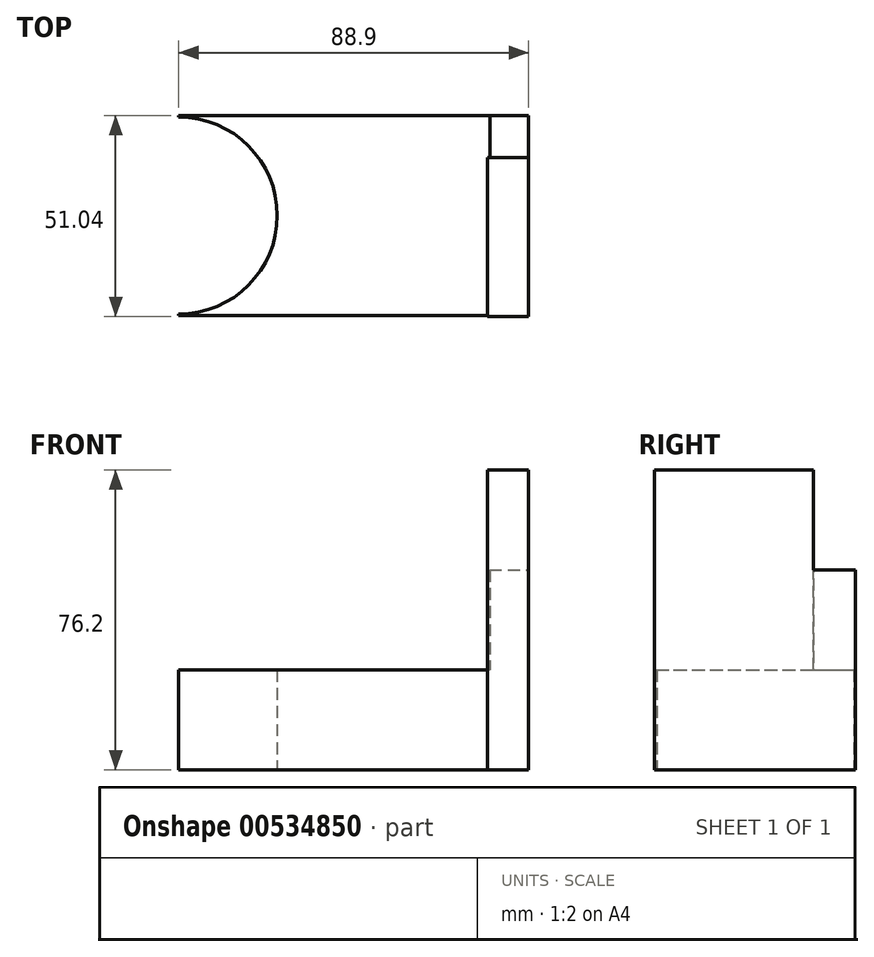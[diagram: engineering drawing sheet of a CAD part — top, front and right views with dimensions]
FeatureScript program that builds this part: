
annotation { "Feature Type Name" : "Feature", "Feature Type Description" : "" }
export const myFeature = defineFeature(function(context is Context, id is Id, definition is map)
    precondition{}
    {
        {
            var Q0;
            Q0=qCreatedBy(makeId("Top.planeOp"),FACE);
            var sketch = newSketch(context, id + "F0", { "sketchPlane" : qUnion([Q0])});
            skLineSegment(sketch, "E0.bottom", {"start": v(44.45, -25.4) * mm, "end": v(-44.45, -25.4) * mm});
            skLineSegment(sketch, "E0.top", {"start": v(44.45, 25.4) * mm, "end": v(-44.45, 25.4) * mm});
            skLineSegment(sketch, "E0.left", {"start": v(44.45, -25.4) * mm, "end": v(44.45, 25.4) * mm});
            skLineSegment(sketch, "E0.right", {"start": v(-44.45, -25.4) * mm, "end": v(-44.45, 25.4) * mm});
            skPoint(sketch, "E0.middle", {"position": v(0, 0) * mm});
            skCircle(sketch, "E1", {"center": v(-44.45, 0) * mm, "radius": 25.05 * mm});
            skSolve(sketch);
        }
        {
            var Q0;
            {var subQ1=sQuery(id+"F0.wireOp",EDGE,"E0.bottom");Q0=makeQuery(id+"F0.imprint","IMPRINT",FACE,{"disambiguationData":[TD([[makeQuery(id+"F0.imprint","IMPRINT",EDGE,{"derivedFrom":subQ1}),-1.0]])]});}
            var Q1;
            {var subQ0=sQuery(id+"F0.wireOp",EDGE,"E1");var subQ1=sQuery(id+"F0.wireOp",EDGE,"E0.right");var subQ2=makeQuery(id+"F0.imprint","INTERSECT",VERTEX,{"disambiguationData":[OD(0.0)],"derivedFrom":[subQ1,subQ0]});Q1=makeQuery(id+"F0.imprint","IMPRINT",FACE,{"disambiguationData":[TD([[makeQuery(id+"F0.imprint","IMPRINT",EDGE,{"disambiguationData":[TD([[subQ2,-1.0]])],"derivedFrom":subQ1}),1.0]])]});}
            var Q2;
            {var subQ0=sQuery(id+"F0.wireOp",EDGE,"E1");var subQ1=sQuery(id+"F0.wireOp",EDGE,"E0.right");var subQ2=makeQuery(id+"F0.imprint","INTERSECT",VERTEX,{"disambiguationData":[OD(0.0)],"derivedFrom":[subQ1,subQ0]});Q2=makeQuery(id+"F0.imprint","IMPRINT",FACE,{"disambiguationData":[TD([[makeQuery(id+"F0.imprint","IMPRINT",EDGE,{"disambiguationData":[TD([[subQ2,-1.0]])],"derivedFrom":subQ1}),-1.0]])]});}
            extrude(context, id + "F1", {"entities" : qUnion([Q0, Q1, Q2]), "depth" : 25.4 * mm, "offsetDistance" : 25.4 * mm});
        }
        {
            var Q0;
            Q0=qCreatedBy(makeId("Top.planeOp"),FACE);
            var sketch = newSketch(context, id + "F2", { "sketchPlane" : qUnion([Q0])});
            skCircle(sketch, "E2", {"center": v(-50.47, 0) * mm, "radius": 11.03 * mm});
            skSolve(sketch);
        }
        {
            var Q0;
            Q0=makeQuery(id+"F2.imprint","IMPRINT",FACE,{"disambiguationData":[TD([[makeQuery(id+"F2.imprint","IMPRINT",EDGE,{"derivedFrom":sQuery(id+"F2.wireOp",EDGE,"E2")}),1.0]])]});
            extrude(context, id + "F3", {"entities" : qUnion([Q0]), "operationType" : NewBodyOperationType.REMOVE, "depth" : 25.4 * mm, "offsetDistance" : 25.4 * mm});
        }
        {
            var Q0;
            Q0=qCreatedBy(makeId("Top.planeOp"),FACE);
            var sketch = newSketch(context, id + "F4", { "sketchPlane" : qUnion([Q0])});
            skLineSegment(sketch, "E3.bottom", {"start": v(34.6, 25.4) * mm, "end": v(44.45, 25.4) * mm});
            skLineSegment(sketch, "E3.top", {"start": v(34.6, 14.73) * mm, "end": v(44.45, 14.73) * mm});
            skLineSegment(sketch, "E3.left", {"start": v(34.6, 25.4) * mm, "end": v(34.6, 14.73) * mm});
            skLineSegment(sketch, "E3.right", {"start": v(44.45, 25.4) * mm, "end": v(44.45, 14.73) * mm});
            skSolve(sketch);
        }
        {
            var Q0;
            Q0=qCreatedBy(makeId("Top.planeOp"),FACE);
            var sketch = newSketch(context, id + "F5", { "sketchPlane" : qUnion([Q0])});
            skLineSegment(sketch, "E4.bottom", {"start": v(33.99, 14.77) * mm, "end": v(44.45, 14.77) * mm});
            skLineSegment(sketch, "E4.top", {"start": v(33.99, -25.64) * mm, "end": v(44.45, -25.64) * mm});
            skLineSegment(sketch, "E4.left", {"start": v(33.99, 14.77) * mm, "end": v(33.99, -25.64) * mm});
            skLineSegment(sketch, "E4.right", {"start": v(44.45, 14.77) * mm, "end": v(44.45, -25.64) * mm});
            skSolve(sketch);
        }
        {
            var Q0;
            Q0=makeQuery(id+"F4.imprint","IMPRINT",FACE,{"disambiguationData":[TD([[makeQuery(id+"F4.imprint","IMPRINT",EDGE,{"derivedFrom":sQuery(id+"F4.wireOp",EDGE,"E3.bottom")}),-1.0]])]});
            extrude(context, id + "F6", {"entities" : qUnion([Q0]), "operationType" : NewBodyOperationType.ADD, "depth" : 50.8 * mm, "offsetDistance" : 25.4 * mm});
        }
        {
            var Q0;
            Q0=makeQuery(id+"F5.imprint","IMPRINT",FACE,{"disambiguationData":[TD([[makeQuery(id+"F5.imprint","IMPRINT",EDGE,{"derivedFrom":sQuery(id+"F5.wireOp",EDGE,"E4.bottom")}),-1.0]])]});
            extrude(context, id + "F7", {"entities" : qUnion([Q0]), "operationType" : NewBodyOperationType.ADD, "depth" : 76.2 * mm, "offsetDistance" : 25.4 * mm});
        }
    });
